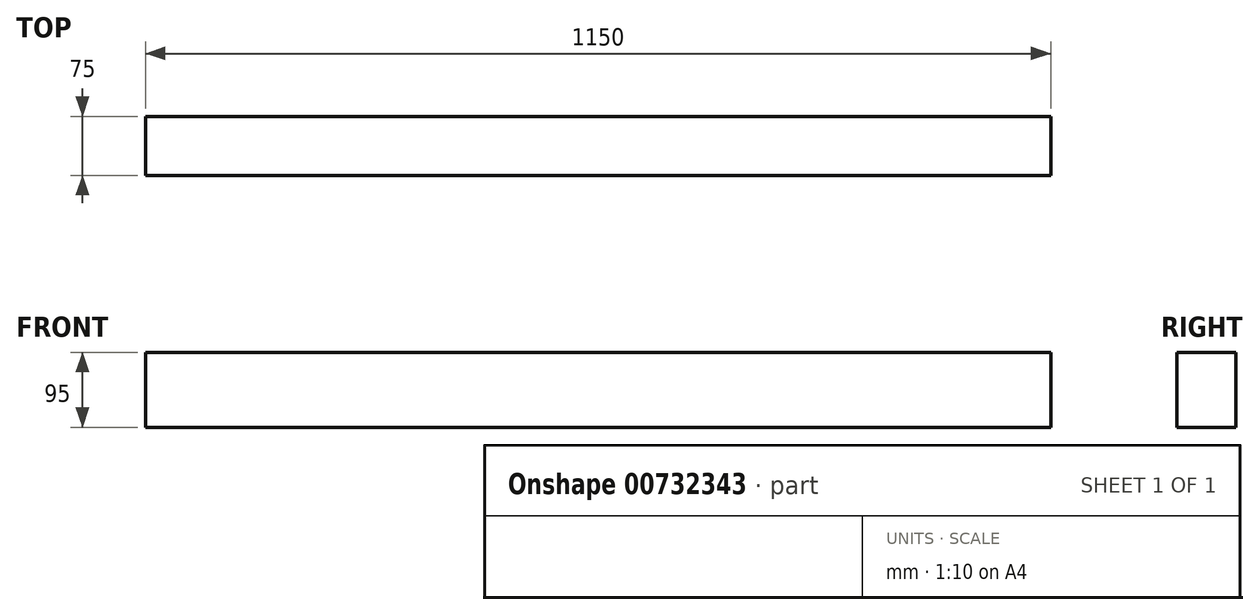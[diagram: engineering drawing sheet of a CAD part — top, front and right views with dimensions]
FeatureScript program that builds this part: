
annotation { "Feature Type Name" : "Feature", "Feature Type Description" : "" }
export const myFeature = defineFeature(function(context is Context, id is Id, definition is map)
    precondition{}
    {
        {
            var Q0;
            Q0=qCreatedBy(makeId("Top.planeOp"),FACE);
            var sketch = newSketch(context, id + "F0", { "sketchPlane" : qUnion([Q0])});
            skLineSegment(sketch, "E0.bottom", {"start": v(-575, 37.5) * mm, "end": v(575, 37.5) * mm});
            skLineSegment(sketch, "E0.top", {"start": v(-575, -37.5) * mm, "end": v(575, -37.5) * mm});
            skLineSegment(sketch, "E0.left", {"start": v(-575, 37.5) * mm, "end": v(-575, -37.5) * mm});
            skLineSegment(sketch, "E0.right", {"start": v(575, 37.5) * mm, "end": v(575, -37.5) * mm});
            skPoint(sketch, "E0.middle", {"position": v(0, 0) * mm});
            skSolve(sketch);
        }
        {
            var Q0;
            Q0=makeQuery(id+"F0.imprint","IMPRINT",FACE,{"disambiguationData":[TD([[makeQuery(id+"F0.imprint","IMPRINT",EDGE,{"derivedFrom":sQuery(id+"F0.wireOp",EDGE,"E0.bottom")}),-1.0]])]});
            extrude(context, id + "F1", {"entities" : qUnion([Q0]), "depth" : 95 * mm, "offsetDistance" : 25 * mm});
        }
    });
